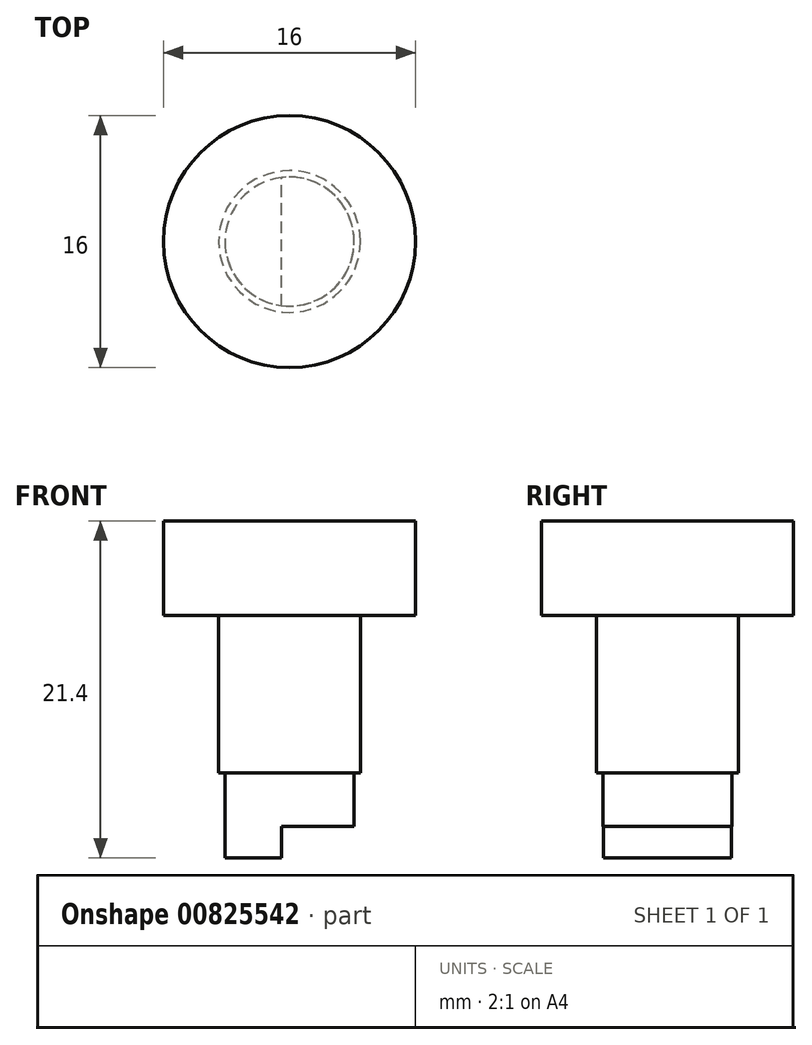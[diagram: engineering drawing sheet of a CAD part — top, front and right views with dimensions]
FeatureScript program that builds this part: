
annotation { "Feature Type Name" : "Feature", "Feature Type Description" : "" }
export const myFeature = defineFeature(function(context is Context, id is Id, definition is map)
    precondition{}
    {
        {
            var Q0;
            Q0=qCreatedBy(makeId("Top.planeOp"),FACE);
            var sketch = newSketch(context, id + "F0", { "sketchPlane" : qUnion([Q0])});
            skCircle(sketch, "E0", {"center": v(0, 0) * mm, "radius": 4.5 * mm});
            skSolve(sketch);
        }
        {
            var Q0;
            Q0=qSketchRegion(id+"F0",true);
            var Q1;
            Q1=makeQuery(id+"F0.imprint","IMPRINT",FACE,{"disambiguationData":[TD([[makeQuery(id+"F0.imprint","IMPRINT",EDGE,{"derivedFrom":sQuery(id+"F0.wireOp",EDGE,"gQIlikyk-XsJC-OwSO-pj1H-ld4xPt6BM2gG")}),1.0]])]});
            extrude(context, id + "F1", {"entities" : qUnion([Q0, Q1]), "depth" : 8 * mm, "offsetDistance" : 25 * mm});
        }
        {
            var Q0;
            Q0=makeQuery(id+"F1.opExtrude","CAP_FACE",FACE,{"disambiguationData":[OSD([sQuery(id+"F0.wireOp",EDGE,"E0")])],"isStart":false});
            var sketch = newSketch(context, id + "F2", { "sketchPlane" : qUnion([Q0])});
            skCircle(sketch, "E1", {"center": v(0, 0) * mm, "radius": 4.5 * mm});
            skSolve(sketch);
        }
        {
            var Q0;
            Q0=qSketchRegion(id+"F2",true);
            extrude(context, id + "F3", {"entities" : qUnion([Q0]), "operationType" : NewBodyOperationType.ADD, "depth" : 2 * mm, "offsetDistance" : 25 * mm});
        }
        {
            var Q0;
            Q0=makeQuery(id+"F3.opExtrude","CAP_FACE",FACE,{"disambiguationData":[OSD([sQuery(id+"F2.wireOp",EDGE,"E1")])],"isStart":false});
            var sketch = newSketch(context, id + "F4", { "sketchPlane" : qUnion([Q0])});
            skCircle(sketch, "E2", {"center": v(0, 0) * mm, "radius": 8 * mm});
            skSolve(sketch);
        }
        {
            var Q0;
            Q0=qSketchRegion(id+"F4",true);
            extrude(context, id + "F5", {"entities" : qUnion([Q0]), "operationType" : NewBodyOperationType.ADD, "depth" : 6 * mm, "offsetDistance" : 25 * mm});
        }
        {
            var Q0;
            Q0=makeQuery(id+"F1.opExtrude","CAP_FACE",FACE,{"disambiguationData":[OSD([sQuery(id+"F0.wireOp",EDGE,"E0"),sQuery(id+"F0.wireOp",EDGE,"G2DXY09y-qrfL-KBHC-DMSi-CX53FLEtt8Pi")])],"isStart":true});
            var sketch = newSketch(context, id + "F6", { "sketchPlane" : qUnion([Q0])});
            skCircle(sketch, "E3", {"center": v(0, 0) * mm, "radius": 4.1 * mm});
            skSolve(sketch);
        }
        {
            var Q0;
            Q0 = qSketchRegion(id + "F6", true);
            extrude(context, id + "F7", {"entities" : qUnion([Q0]), "operationType" : NewBodyOperationType.ADD, "depth" : 3.4 * mm, "offsetDistance" : 25 * mm});
        }
        {
            var Q0;
            Q0=makeQuery(id+"F7.opExtrude","CAP_FACE",FACE,{"disambiguationData":[OSD([sQuery(id+"F6.wireOp",EDGE,"E3")])],"isStart":false});
            var sketch = newSketch(context, id + "F8", { "sketchPlane" : qUnion([Q0])});
            skCircle(sketch, "E4", {"center": v(0, 0) * mm, "radius": 4.1 * mm});
            skLineSegment(sketch, "E5", {"start": v(0, 0) * mm, "end": v(-0.5, 4.07) * mm});
            skLineSegment(sketch, "E6", {"start": v(-0.5, 4.07) * mm, "end": v(-0.5, 0) * mm});
            skLineSegment(sketch, "E7.MirrorCS", {"start": v(-0.5, -4.07) * mm, "end": v(-0.5, 0) * mm});
            skSolve(sketch);
        }
        {
            var Q0;
            {var subQ0=sQuery(id+"F8.wireOp",EDGE,"E6");Q0=makeQuery(id+"F8.imprint","IMPRINT",FACE,{"disambiguationData":[TD([[makeQuery(id+"F8.imprint","IMPRINT",EDGE,{"derivedFrom":subQ0}),-1.0]])]});}
            extrude(context, id + "F9", {"entities" : qUnion([Q0]), "operationType" : NewBodyOperationType.ADD, "depth" : 2 * mm, "offsetDistance" : 25 * mm});
        }
    });
